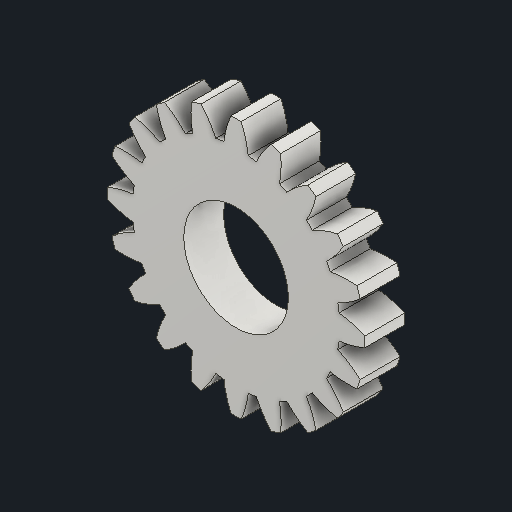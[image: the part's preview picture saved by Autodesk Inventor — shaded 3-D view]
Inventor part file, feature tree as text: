
AUTODESK INVENTOR PART (.ipt)
format: ipt  version: 2025.3 (Build 293356030, 356C)  size: 244,736 bytes
history: native  units: mm (DEFAULTED — no unit token found)
features: plane x3, other x3, extrude x2, sketch x2
ambient origin geometry x8: Origin, YZ Plane, XZ Plane, XY Plane, X Axis, Y Axis, Z Axis, Center Point
bodies: Solid1 (feature_tree)
feature tree (10):
  extrude  "Extrusion1"  Depth=4.0mm TaperAngle=0.0deg
  plane  "Work Plane2"
  plane  "Work Plane8"
  plane  "Work Plane9"
  other  "Spur Gear"
  extrude  "Extrusion2"  Depth=10.0mm TaperAngle=0.0deg
  sketch  "Sketch1"  dims[d0=25.874266mm d1=4.0mm d2=0.0mm]
  other  "Srf1"
  sketch  "Sketch3"  dims[d3=22.5mm d4=10.0mm d5=0.0mm d16=40.0mm d17=0.0mm d34=1.570796mm d39=0.0mm d41=0.0mm d43=40.0mm d46=40.0mm d47=0.0mm d48=0.0mm d49=10.5mm d50=10.0mm d51=0.0mm]
  other  "Pitch Diameter"
